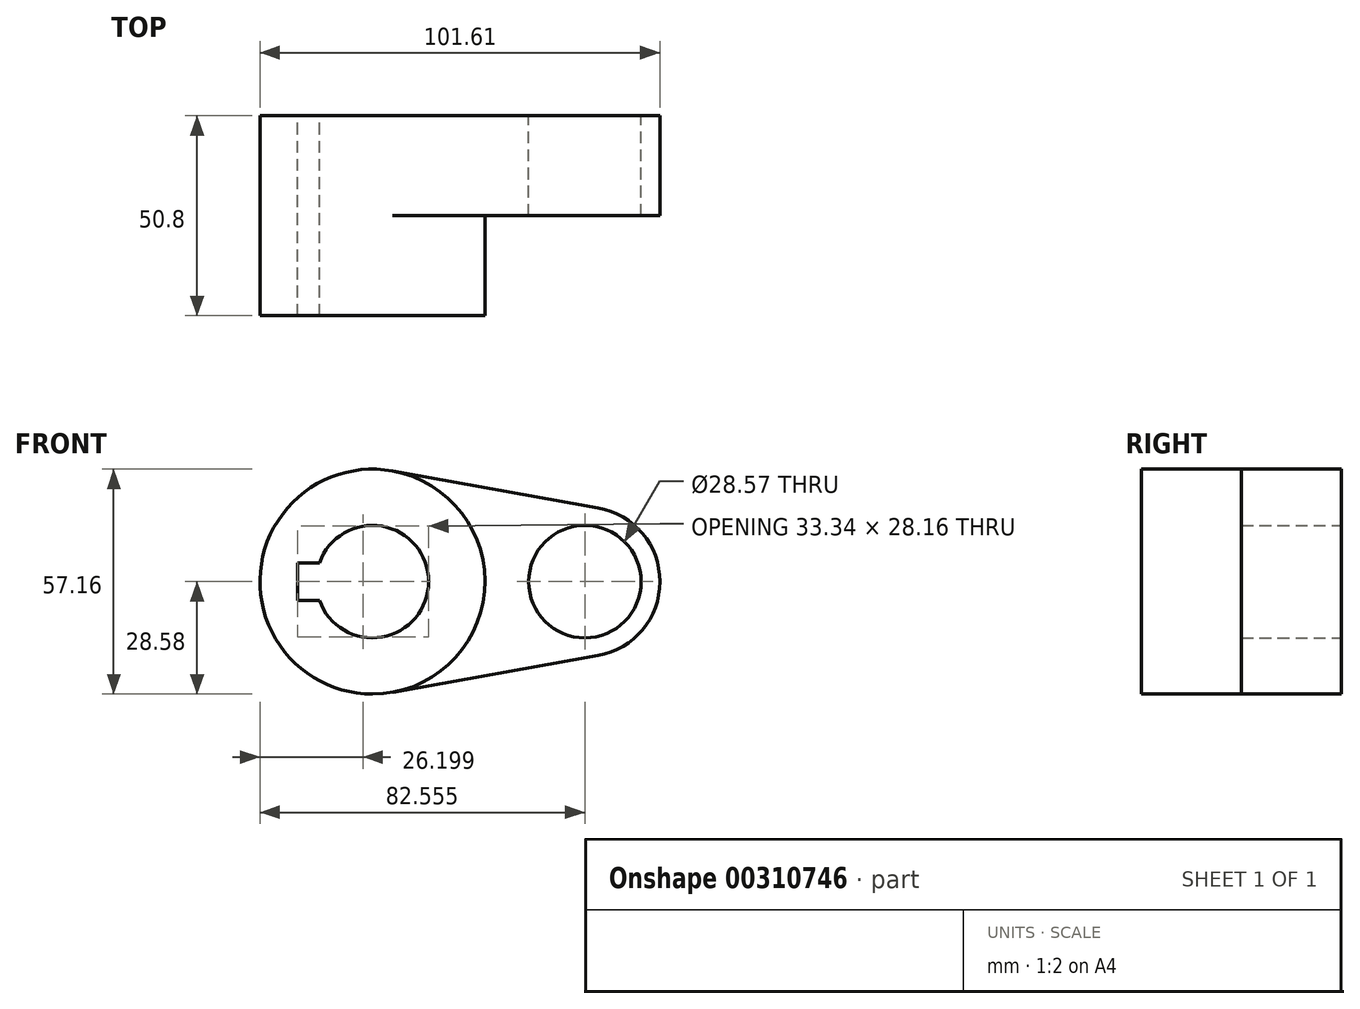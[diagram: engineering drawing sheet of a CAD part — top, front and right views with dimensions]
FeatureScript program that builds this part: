
annotation { "Feature Type Name" : "Feature", "Feature Type Description" : "" }
export const myFeature = defineFeature(function(context is Context, id is Id, definition is map)
    precondition{}
    {
        {
            var Q0;
            Q0=qCreatedBy(makeId("Front.planeOp"),FACE);
            var sketch = newSketch(context, id + "F0", { "sketchPlane" : qUnion([Q0])});
            skCircle(sketch, "E0", {"center": v(0, 0) * mm, "radius": 28.57 * mm});
            skCircle(sketch, "E1", {"center": v(53.98, 0) * mm, "radius": 19.05 * mm});
            skLineSegment(sketch, "E2", {"start": v(5.04, 28.13) * mm, "end": v(57.34, 18.75) * mm});
            skLineSegment(sketch, "E3", {"start": v(5.04, -28.13) * mm, "end": v(57.34, -18.75) * mm});
            skCircle(sketch, "E4", {"center": v(0, 0) * mm, "radius": 14.29 * mm});
            skCircle(sketch, "E5", {"center": v(53.98, 0) * mm, "radius": 14.29 * mm});
            skLineSegment(sketch, "E6.bottom", {"start": v(19.05, 4.76) * mm, "end": v(-19.05, 4.76) * mm});
            skLineSegment(sketch, "E6.top", {"start": v(19.05, -4.76) * mm, "end": v(-19.05, -4.76) * mm});
            skLineSegment(sketch, "E6.left", {"start": v(19.05, 4.76) * mm, "end": v(19.05, -4.76) * mm});
            skLineSegment(sketch, "E6.right", {"start": v(-19.05, 4.76) * mm, "end": v(-19.05, -4.76) * mm});
            skSolve(sketch);
        }
        {
            var Q0;
            {var subQ0=sQuery(id+"F0.wireOp",EDGE,"E2");Q0=makeQuery(id+"F0.imprint","IMPRINT",FACE,{"disambiguationData":[TD([[makeQuery(id+"F0.imprint","IMPRINT",EDGE,{"derivedFrom":subQ0}),-1.0]])]});}
            var Q1;
            Q1=makeQuery(id+"F0.imprint","IMPRINT",FACE,{"disambiguationData":[TD([[makeQuery(id+"F0.imprint","IMPRINT",EDGE,{"derivedFrom":sQuery(id+"F0.wireOp",EDGE,"E5")}),-1.0]])]});
            var Q2;
            {var subQ7=sQuery(id+"F0.wireOp",EDGE,"E6.left");Q2=makeQuery(id+"F0.imprint","IMPRINT",FACE,{"disambiguationData":[TD([[makeQuery(id+"F0.imprint","IMPRINT",EDGE,{"derivedFrom":subQ7}),1.0]])]});}
            var Q3;
            {var subQ5=sQuery(id+"F0.wireOp",EDGE,"E6.left");Q3=makeQuery(id+"F0.imprint","IMPRINT",FACE,{"disambiguationData":[TD([[makeQuery(id+"F0.imprint","IMPRINT",EDGE,{"derivedFrom":subQ5}),-1.0]])]});}
            extrude(context, id + "F1", {"entities" : qUnion([Q0, Q1, Q2, Q3]), "offsetDistance" : 25.4 * mm, "depth" : 25.4 * mm});
        }
        {
            var Q0;
            {var subQ7=sQuery(id+"F0.wireOp",EDGE,"E6.left");Q0=makeQuery(id+"F0.imprint","IMPRINT",FACE,{"disambiguationData":[TD([[makeQuery(id+"F0.imprint","IMPRINT",EDGE,{"derivedFrom":subQ7}),1.0]])]});}
            var Q1;
            {var subQ5=sQuery(id+"F0.wireOp",EDGE,"E6.left");Q1=makeQuery(id+"F0.imprint","IMPRINT",FACE,{"disambiguationData":[TD([[makeQuery(id+"F0.imprint","IMPRINT",EDGE,{"derivedFrom":subQ5}),-1.0]])]});}
            extrude(context, id + "F2", {"entities" : qUnion([Q0, Q1]), "operationType" : NewBodyOperationType.ADD, "offsetDistance" : 25.4 * mm, "depth" : 50.8 * mm});
        }
    });
